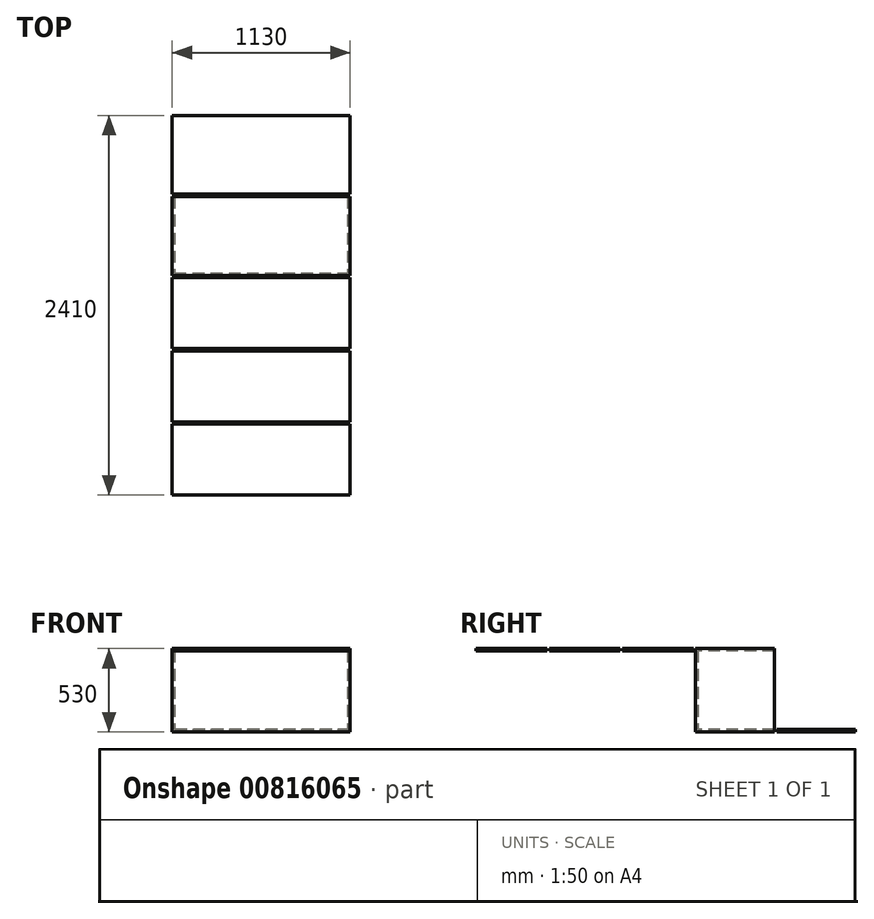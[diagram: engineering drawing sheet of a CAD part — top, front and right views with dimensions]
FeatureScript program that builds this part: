
annotation { "Feature Type Name" : "Feature", "Feature Type Description" : "" }
export const myFeature = defineFeature(function(context is Context, id is Id, definition is map)
    precondition{}
    {
        {
            var Q0;
            Q0=qCreatedBy(makeId("Front.planeOp"),FACE);
            var sketch = newSketch(context, id + "F0", { "sketchPlane" : qUnion([Q0])});
            skLineSegment(sketch, "E0.bottom", {"start": v(-560.03, 220.66) * mm, "end": v(539.97, 220.66) * mm});
            skLineSegment(sketch, "E0.top", {"start": v(-560.03, -279.34) * mm, "end": v(539.97, -279.34) * mm});
            skLineSegment(sketch, "E0.left", {"start": v(-560.03, 220.66) * mm, "end": v(-560.03, -279.34) * mm});
            skLineSegment(sketch, "E0.right", {"start": v(539.97, 220.66) * mm, "end": v(539.97, -279.34) * mm});
            skSolve(sketch);
        }
        {
            var Q0;
            Q0 = qSketchRegion(id + "F0", true);
            extrude(context, id + "F1", {"entities" : qUnion([Q0]), "depth" : 15 * mm, "offsetDistance" : 25 * mm});
        }
        {
            var Q0;
            Q0=makeQuery(id+"F1.opExtrude","CAP_FACE",FACE,{"disambiguationData":[OSD([sQuery(id+"F0.wireOp",EDGE,"E0.bottom"),sQuery(id+"F0.wireOp",EDGE,"E0.top"),sQuery(id+"F0.wireOp",EDGE,"E0.left"),sQuery(id+"F0.wireOp",EDGE,"E0.right")])],"isStart":false});
            var sketch = newSketch(context, id + "F2", { "sketchPlane" : qUnion([Q0])});
            skLineSegment(sketch, "E1.bottom", {"start": v(554.97, -279.34) * mm, "end": v(539.97, -279.34) * mm});
            skLineSegment(sketch, "E1.top", {"start": v(554.97, 220.66) * mm, "end": v(539.97, 220.66) * mm});
            skLineSegment(sketch, "E1.left", {"start": v(554.97, -279.34) * mm, "end": v(554.97, 220.66) * mm});
            skLineSegment(sketch, "E1.right", {"start": v(539.97, -279.34) * mm, "end": v(539.97, 220.66) * mm});
            skLineSegment(sketch, "E2.bottom", {"start": v(-560.03, -279.34) * mm, "end": v(-575.03, -279.34) * mm});
            skLineSegment(sketch, "E2.top", {"start": v(-560.03, 220.66) * mm, "end": v(-575.03, 220.66) * mm});
            skLineSegment(sketch, "E2.left", {"start": v(-560.03, -279.34) * mm, "end": v(-560.03, 220.66) * mm});
            skLineSegment(sketch, "E2.right", {"start": v(-575.03, -279.34) * mm, "end": v(-575.03, 220.66) * mm});
            skSolve(sketch);
        }
        {
            var Q0;
            Q0 = qSketchRegion(id + "F2", true);
            extrude(context, id + "F3", {"entities" : qUnion([Q0]), "operationType" : NewBodyOperationType.ADD, "oppositeDirection" : true, "depth" : 500 * mm, "offsetDistance" : 25 * mm});
        }
        {
            var Q0;
            Q0=makeQuery(id+"F3.boolean.opBoolean","MERGE",FACE,{"derivedFrom":[makeQuery(id+"F1.opExtrude","SWEPT_FACE",FACE,{"disambiguationData":[OSD([sQuery(id+"F0.wireOp",EDGE,"E0.top")])]}),makeQuery(id+"F3.opExtrude","SWEPT_FACE",FACE,{"disambiguationData":[OSD([sQuery(id+"F2.wireOp",EDGE,"E1.bottom")])]}),makeQuery(id+"F3.opExtrude","SWEPT_FACE",FACE,{"disambiguationData":[OSD([sQuery(id+"F2.wireOp",EDGE,"E2.bottom")])]})]});
            var sketch = newSketch(context, id + "F4", { "sketchPlane" : qUnion([Q0])});
            skLineSegment(sketch, "E3.bottom", {"start": v(-575.03, 15) * mm, "end": v(554.97, 15) * mm});
            skLineSegment(sketch, "E3.top", {"start": v(-575.03, -485) * mm, "end": v(554.97, -485) * mm});
            skLineSegment(sketch, "E3.left", {"start": v(-575.03, 15) * mm, "end": v(-575.03, -485) * mm});
            skLineSegment(sketch, "E3.right", {"start": v(554.97, 15) * mm, "end": v(554.97, -485) * mm});
            skSolve(sketch);
        }
        {
            var Q0;
            Q0 = qSketchRegion(id + "F4", true);
            extrude(context, id + "F5", {"entities" : qUnion([Q0]), "operationType" : NewBodyOperationType.ADD, "depth" : 15 * mm, "offsetDistance" : 25 * mm});
        }
        {
            var Q0;
            Q0=makeQuery(id+"F3.boolean.opBoolean","MERGE",FACE,{"derivedFrom":[makeQuery(id+"F1.opExtrude","SWEPT_FACE",FACE,{"disambiguationData":[OSD([sQuery(id+"F0.wireOp",EDGE,"E0.bottom")])]}),makeQuery(id+"F3.opExtrude","SWEPT_FACE",FACE,{"disambiguationData":[OSD([sQuery(id+"F2.wireOp",EDGE,"E1.top")])]}),makeQuery(id+"F3.opExtrude","SWEPT_FACE",FACE,{"disambiguationData":[OSD([sQuery(id+"F2.wireOp",EDGE,"E2.top")])]})]});
            var sketch = newSketch(context, id + "F6", { "sketchPlane" : qUnion([Q0])});
            skLineSegment(sketch, "E4.bottom", {"start": v(-575.03, 485) * mm, "end": v(554.97, 485) * mm});
            skLineSegment(sketch, "E4.top", {"start": v(-575.03, -15) * mm, "end": v(554.97, -15) * mm});
            skLineSegment(sketch, "E4.left", {"start": v(-575.03, 485) * mm, "end": v(-575.03, -15) * mm});
            skLineSegment(sketch, "E4.right", {"start": v(554.97, 485) * mm, "end": v(554.97, -15) * mm});
            skSolve(sketch);
        }
        {
            var Q0;
            Q0 = qSketchRegion(id + "F6", true);
            extrude(context, id + "F7", {"entities" : qUnion([Q0]), "operationType" : NewBodyOperationType.ADD, "depth" : 15 * mm, "offsetDistance" : 25 * mm});
        }
        {
            var Q0;
            Q0=makeQuery(id+"F7.boolean.opBoolean","MERGE",FACE,{"derivedFrom":[makeQuery(id+"F5.boolean.opBoolean","MERGE",FACE,{"derivedFrom":[makeQuery(id+"F3.opExtrude","CAP_FACE",FACE,{"disambiguationData":[OSD([sQuery(id+"F2.wireOp",EDGE,"E1.bottom"),sQuery(id+"F2.wireOp",EDGE,"E1.top"),sQuery(id+"F2.wireOp",EDGE,"E1.left"),sQuery(id+"F2.wireOp",EDGE,"E1.right")])],"isStart":false}),makeQuery(id+"F3.opExtrude","CAP_FACE",FACE,{"disambiguationData":[OSD([sQuery(id+"F2.wireOp",EDGE,"E2.bottom"),sQuery(id+"F2.wireOp",EDGE,"E2.top"),sQuery(id+"F2.wireOp",EDGE,"E2.left"),sQuery(id+"F2.wireOp",EDGE,"E2.right")])],"isStart":false}),makeQuery(id+"F5.opExtrude","SWEPT_FACE",FACE,{"disambiguationData":[OSD([sQuery(id+"F4.wireOp",EDGE,"E3.top")])]})]}),makeQuery(id+"F7.opExtrude","SWEPT_FACE",FACE,{"disambiguationData":[OSD([sQuery(id+"F6.wireOp",EDGE,"E4.bottom")])]})]});
            var sketch = newSketch(context, id + "F8", { "sketchPlane" : qUnion([Q0])});
            skLineSegment(sketch, "E5.bottom", {"start": v(-554.97, -294.34) * mm, "end": v(575.03, -294.34) * mm});
            skLineSegment(sketch, "E5.top", {"start": v(-554.97, -279.73) * mm, "end": v(575.03, -279.73) * mm});
            skLineSegment(sketch, "E5.left", {"start": v(-554.97, -279.73) * mm, "end": v(-554.97, -294.34) * mm});
            skLineSegment(sketch, "E5.right", {"start": v(575.03, -279.73) * mm, "end": v(575.03, -294.34) * mm});
            skSolve(sketch);
        }
        {
            var Q0;
            Q0 = qSketchRegion(id + "F8", true);
            extrude(context, id + "F9", {"entities" : qUnion([Q0]), "depth" : 500 * mm, "offsetDistance" : 25 * mm});
        }
        {
            var Q0;
            Q0=makeQuery(id+"F9.opExtrude","SWEPT_BODY",BODY,{"disambiguationData":[OSD([sQuery(id+"F8.wireOp",EDGE,"E5.bottom"),sQuery(id+"F8.wireOp",EDGE,"E5.top"),sQuery(id+"F8.wireOp",EDGE,"E5.left"),sQuery(id+"F8.wireOp",EDGE,"E5.right")])]});
            var Q1;
            Q1=makeQuery(id+"F7.opExtrude","CAP_EDGE",EDGE,{"disambiguationData":[OSD([sQuery(id+"F6.wireOp",EDGE,"E4.left")])],"isStart":false});
            transform(context, id + "F10", {"entities" : qUnion([Q0]), "transformType" : TransformType.TRANSLATION_DISTANCE, "transformDirection" : qUnion([Q1]), "distance" : 15 * mm, "oppositeDirection" : true, "makeCopy" : false});
        }
        {
            var Q0;
            Q0=makeQuery(id+"F7.opExtrude","CAP_FACE",FACE,{"disambiguationData":[OSD([sQuery(id+"F6.wireOp",EDGE,"E4.bottom"),sQuery(id+"F6.wireOp",EDGE,"E4.top"),sQuery(id+"F6.wireOp",EDGE,"E4.left"),sQuery(id+"F6.wireOp",EDGE,"E4.right")])],"isStart":false});
            var sketch = newSketch(context, id + "F11", { "sketchPlane" : qUnion([Q0])});
            skLineSegment(sketch, "E6.bottom", {"start": v(554.97, -30) * mm, "end": v(-575.03, -30) * mm});
            skLineSegment(sketch, "E6.top", {"start": v(554.97, -480) * mm, "end": v(-575.03, -480) * mm});
            skLineSegment(sketch, "E6.left", {"start": v(554.97, -30) * mm, "end": v(554.97, -480) * mm});
            skLineSegment(sketch, "E6.right", {"start": v(-575.03, -30) * mm, "end": v(-575.03, -480) * mm});
            skSolve(sketch);
        }
        {
            var Q0;
            Q0=makeQuery(id+"F11.imprint","IMPRINT",FACE,{"disambiguationData":[TD([[makeQuery(id+"F11.imprint","IMPRINT",EDGE,{"derivedFrom":sQuery(id+"F11.wireOp",EDGE,"E6.bottom")}),1.0]])]});
            extrude(context, id + "F12", {"entities" : qUnion([Q0]), "oppositeDirection" : true, "depth" : 15 * mm, "offsetDistance" : 25 * mm});
        }
        {
            var Q0;
            Q0=makeQuery(id+"F12.opExtrude","CAP_FACE",FACE,{"disambiguationData":[OSD([sQuery(id+"F11.wireOp",EDGE,"E6.bottom"),sQuery(id+"F11.wireOp",EDGE,"E6.top"),sQuery(id+"F11.wireOp",EDGE,"E6.left"),sQuery(id+"F11.wireOp",EDGE,"E6.right")])],"isStart":true});
            var sketch = newSketch(context, id + "F13", { "sketchPlane" : qUnion([Q0])});
            skLineSegment(sketch, "E7.bottom", {"start": v(-575.03, -495) * mm, "end": v(554.97, -495) * mm});
            skLineSegment(sketch, "E7.top", {"start": v(-575.03, -945) * mm, "end": v(554.97, -945) * mm});
            skLineSegment(sketch, "E7.left", {"start": v(-575.03, -495) * mm, "end": v(-575.03, -945) * mm});
            skLineSegment(sketch, "E7.right", {"start": v(554.97, -495) * mm, "end": v(554.97, -945) * mm});
            skSolve(sketch);
        }
        {
            var Q0;
            Q0=makeQuery(id+"F13.imprint","IMPRINT",FACE,{"disambiguationData":[TD([[makeQuery(id+"F13.imprint","IMPRINT",EDGE,{"derivedFrom":sQuery(id+"F13.wireOp",EDGE,"E7.bottom")}),-1.0]])]});
            extrude(context, id + "F14", {"entities" : qUnion([Q0]), "oppositeDirection" : true, "depth" : 15 * mm, "offsetDistance" : 25 * mm});
        }
        {
            var Q0;
            Q0=makeQuery(id+"F14.opExtrude","CAP_FACE",FACE,{"disambiguationData":[OSD([sQuery(id+"F13.wireOp",EDGE,"E7.bottom"),sQuery(id+"F13.wireOp",EDGE,"E7.top"),sQuery(id+"F13.wireOp",EDGE,"E7.left"),sQuery(id+"F13.wireOp",EDGE,"E7.right")])],"isStart":true});
            var sketch = newSketch(context, id + "F15", { "sketchPlane" : qUnion([Q0])});
            skLineSegment(sketch, "E8.bottom", {"start": v(-575.03, -960) * mm, "end": v(554.97, -960) * mm});
            skLineSegment(sketch, "E8.top", {"start": v(-575.03, -1410) * mm, "end": v(554.97, -1410) * mm});
            skLineSegment(sketch, "E8.left", {"start": v(-575.03, -960) * mm, "end": v(-575.03, -1410) * mm});
            skLineSegment(sketch, "E8.right", {"start": v(554.97, -960) * mm, "end": v(554.97, -1410) * mm});
            skSolve(sketch);
        }
        {
            var Q0;
            Q0=makeQuery(id+"F15.imprint","IMPRINT",FACE,{"disambiguationData":[TD([[makeQuery(id+"F15.imprint","IMPRINT",EDGE,{"derivedFrom":sQuery(id+"F15.wireOp",EDGE,"E8.bottom")}),-1.0]])]});
            extrude(context, id + "F16", {"entities" : qUnion([Q0]), "oppositeDirection" : true, "depth" : 15 * mm, "offsetDistance" : 25 * mm});
        }
    });
